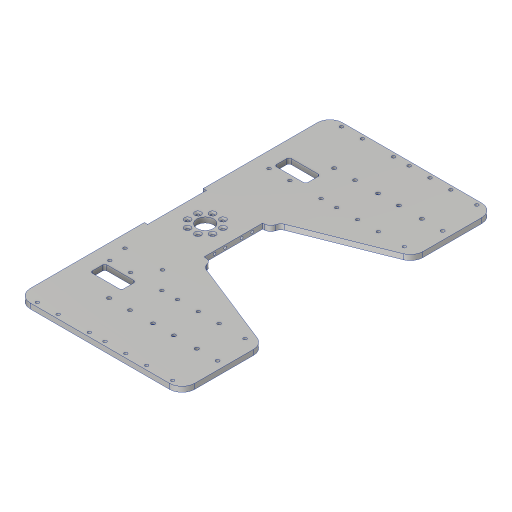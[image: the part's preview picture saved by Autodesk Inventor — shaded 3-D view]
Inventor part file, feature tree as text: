
AUTODESK INVENTOR PART (.ipt)
format: ipt  version: 2023.2 (Build 272271000, 271)  size: 1,916,928 bytes
history: native  units: mm
features: extrude x45, sketch x38, projected_geometry x37, fillet x9, other x7, mirror x6, reference x4, chamfer x3
ambient origin geometry x8: Origin, YZ Plane, XZ Plane, XY Plane, X Axis, Y Axis, Z Axis, Center Point
bodies: Body1 (feature_tree)
feature tree (149):
  other  "솔리드1"
  extrude  "돌출1"  Depth=54.2mm
  sketch  "스케치3"
  extrude  "돌출4"  Depth=56.0mm
  extrude  "돌출5"  Depth=27.1mm
  extrude  "돌출6"  Depth=28.0mm
  extrude  "돌출7"  Depth=5.0mm TaperAngle=0.0deg
  chamfer  "모따기1"  Distance=16.0mm
  extrude  "돌출8"  Depth=2.0mm TaperAngle=0.0deg
  extrude  "돌출9"  Depth=2.5mm
  extrude  "돌출13"  Depth=2.5mm
  extrude  "돌출14"  Depth=2.5mm
  extrude  "돌출15"  Depth=2.5mm
  chamfer  "모따기3"  Distance=2.5mm
  extrude  "돌출16"  Depth=2.5mm
  fillet  "모깎기2"  Radius=2.5mm
  sketch  "스케치17"
  extrude  "돌출17"  Depth=2.5mm
  extrude  "돌출18"  Depth=10.0mm
  extrude  "돌출19"  Depth=20.0mm
  extrude  "돌출20"  Depth=20.0mm
  fillet  "모깎기3"  Radius=10.0mm
  extrude  "돌출21"  Depth=8.0mm TaperAngle=0.0deg
  sketch  "스케치21"
  extrude  "돌출22"  Depth=8.0mm TaperAngle=0.0deg
  extrude  "돌출23"  Depth=13.0mm
  sketch  "스케치22"
  extrude  "돌출24"  TaperAngle=22.5deg  [1 undecoded]
  extrude  "돌출25"  Depth=3.2mm
  sketch  "스케치23"
  extrude  "돌출26"  Depth=80.0mm TaperAngle=360.0deg
  extrude  "돌출27"  Depth=10.0mm TaperAngle=0.0deg
  sketch  "스케치25"
  extrude  "돌출28"  Depth=2.0mm TaperAngle=45.0deg
  extrude  "돌출29"  Depth=5.0mm TaperAngle=0.0deg
  fillet  "모깎기4"  Radius=5.0mm
  extrude  "돌출30"  Depth=500.0mm TaperAngle=0.0deg
  extrude  "돌출31"  Depth=5.0mm TaperAngle=0.0deg
  extrude  "돌출32"  Depth=5.0mm TaperAngle=0.0deg
  extrude  "돌출33"  Depth=2.0mm TaperAngle=45.0deg
  fillet  "모깎기5"  Radius=10.0mm
  extrude  "돌출34"  Depth=2.0mm
  extrude  "돌출35"  Depth=2.0mm
  extrude  "돌출36"  Depth=10.0mm TaperAngle=0.0deg
  fillet  "모깎기7"  Radius=10.0mm
  extrude  "돌출37"  Depth=30.0mm
  extrude  "돌출38"  Depth=10.0mm TaperAngle=0.0deg
  mirror  "미러1"
  mirror  "미러2"
  mirror  "미러3"
  fillet  "모깎기8"  Radius=20.0mm
  extrude  "돌출39"  Depth=40.0mm
  extrude  "돌출40"  Depth=10.0mm TaperAngle=0.0deg
  extrude  "돌출41"  Depth=2.0mm
  extrude  "돌출42"  Depth=3.2mm
  mirror  "미러4"
  chamfer  "모따기4"  Distance=3.2mm
  extrude  "돌출43"  Depth=20.0mm
  extrude  "돌출44"  Depth=3.2mm
  extrude  "돌출45"  Depth=3.2mm
  extrude  "돌출46"  Depth=3.2mm
  extrude  "돌출47"  Depth=30.0mm
  fillet  "모깎기9"  Radius=20.0mm
  fillet  "모깎기10"  Radius=3.2mm
  extrude  "돌출48"  Depth=20.0mm
  sketch  "스케치49"
  extrude  "돌출49"  Depth=8.0mm
  extrude  "돌출50"  Depth=14.0mm
  mirror  "미러5"
  mirror  "미러6"
  fillet  "모깎기11"  Radius=16.501mm
  sketch  "스케치1"
  sketch  "스케치4"
  projected_geometry  "투영된 루프2"
  sketch  "스케치5"
  projected_geometry  "투영된 루프3"
  sketch  "스케치6"
  projected_geometry  "투영된 루프4"
  sketch  "스케치7"
  projected_geometry  "투영된 루프5"
  sketch  "스케치9"
  projected_geometry  "투영된 루프7"
  reference  "참조2"
  sketch  "스케치13"
  projected_geometry  "투영된 루프10"
  sketch  "스케치14"
  projected_geometry  "투영된 루프11"
  projected_geometry  "투영된 루프12"
  reference  "참조3"
  reference  "참조4"
  sketch  "스케치15"
  projected_geometry  "투영된 루프13"
  projected_geometry  "투영된 루프14"
  reference  "참조5"
  projected_geometry  "투영된 루프15"
  sketch  "스케치18"
  projected_geometry  "투영된 루프16"
  sketch  "스케치19"
  projected_geometry  "투영된 루프17"
  sketch  "스케치20"
  projected_geometry  "투영된 루프18"
  projected_geometry  "투영된 루프19"
  projected_geometry  "투영된 루프20"
  projected_geometry  "투영된 루프21"
  projected_geometry  "투영된 루프22"
  sketch  "스케치26"
  projected_geometry  "투영된 루프23"
  sketch  "스케치27"
  projected_geometry  "투영된 루프24"
  sketch  "스케치28"
  projected_geometry  "투영된 루프25"
  sketch  "스케치29"
  projected_geometry  "투영된 루프26"
  sketch  "스케치30"
  projected_geometry  "투영된 루프27"
  sketch  "스케치31"
  projected_geometry  "투영된 루프28"
  sketch  "스케치32"
  sketch  "스케치33"
  projected_geometry  "투영된 루프29"
  sketch  "스케치34"
  projected_geometry  "투영된 루프30"
  sketch  "스케치35"
  projected_geometry  "투영된 루프31"
  sketch  "스케치36"
  projected_geometry  "투영된 루프32"
  sketch  "스케치39"
  projected_geometry  "투영된 루프33"
  sketch  "스케치40"
  projected_geometry  "투영된 루프34"
  sketch  "스케치41"
  projected_geometry  "투영된 루프35"
  sketch  "스케치42"
  projected_geometry  "투영된 루프36"
  sketch  "스케치44"
  projected_geometry  "투영된 루프38"
  sketch  "스케치45"
  projected_geometry  "투영된 루프39"
  sketch  "스케치47"
  projected_geometry  "투영된 루프41"
  sketch  "스케치48"
  projected_geometry  "투영된 루프42"
  projected_geometry  "투영된 루프43"
  other  "<userpath>\Desktop\2022 manipulator (국방로봇)\JWM.iam"
  other  "JWM.iam"
  other  "기어2:8"
  other  "너트6:4"
  other  "너트6:1"
  other  "큰기어고정부:2"
note: 1 required parameter value undecoded (feature->parameter linkage not recoverable at this tier; creation-order binding heuristic only, values carry confidence <= 0.55)
